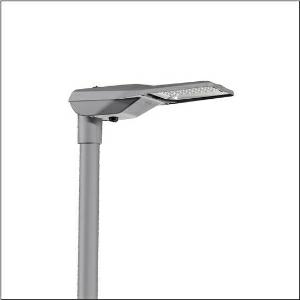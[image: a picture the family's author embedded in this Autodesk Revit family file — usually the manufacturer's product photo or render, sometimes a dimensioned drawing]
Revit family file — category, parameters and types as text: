
# Revit family: streetlight_sl_21_iq_mini___p0_8ab_5xe2r31y08gb_b9a0
name_source: partatom
category: Lighting Fixtures
units: mm (PartAtom-declared; Revit-internal decimal feet)

## family parameters
Cut with Voids When Loaded = No
Host = Face
Light Source = No
Part Type = Normal
Room Calculation Point = No
Round Connector Dimension = Use Diameter
Shared = No

## types (1)
- --- (1 x LED, 5200 lm, 39.8 W, 3000K)
    Apparent Load = 40 VA
    CIE Flux Codes = 36 71 98 100 100
    Color Rendering = 70
    Color Temperature = 3000K
    Default Elevation = 1800 mm
    Description = Streetlight SL 21 iQ mini, mast luminaire, primary light control with lens, of PMMA, primary optical cover: cover, of toughened safety glass, transparent, light distribution: P0.8aB, light emission: direct distribution, primary light characteristic: asymmetric, installation type: post-top, side-entry, LED, High Power LED, rated luminous flux: 5.200lm, luminous efficacy: 131lm/W, light colour: 730, colour temperature: 3000K, control gear: iQ-Street Remote, D4i with power reduction, control: pre-setting: logarithmic dimming characteristic, Street-Remote, Auto-Match, Temp-Guard, Lumen-Switch, Night-Set, Smart-Wire, Light-Fading, Desk-Remote (wireless, voltage-free reading and setting of iQ features in the workshop via application-optimized NFC function/RFID function), optimised constant luminous flux control (CLO 2.0), mains connection: 220..240V, AC, 50/60Hz, start of lifetime: 40W, end of service life: 41W, reduction: 18W, luminaire housing, of diecast aluminium, powder-coated, Siteco® metallic grey (DB 702S), corrosivity category C5 mid according to DIN EN ISO 12944, please order mast flange separately, inclination adjustable: 0°, 5°, 10°, 15°, sealing non-destructively replaceable, multi-level sealing system, length: 628mm, width: 235mm, height: 110mm, mast flange for spigot size: 42mm (side-entry): 5XC10008XM4, 60/48mm (side-entry/post-top): 5XC10108XM2, 76/60mm (side-entry/post-top): 5XC10108XM1, mounting height: 4..8m, Smart Interface below and above, protection rating (complete): IP66, insulation class (complete): insulation class II (safety insulation), certification: CE, ENEC, ENEC+, VDE, impact resistance: IK09, permissible operating ambient temperature for outdoor applications: -40..+50°C, standard-compliant lighting for roads and squares, packaging unit: 1 piece

Light Distribution: P0.8aB
    Height = 110 mm
    Lamp = 1 x LED
    Lamp Light Flux = 5200 lm
    Lamp Power = 39.8 W
    Lamp count = 1
    Length = 625 mm
    Luminous efficacy = 131 lm/W
    Manufacturer = Siteco
    ModVariant = No
    Model = 5XE2R31Y08GB
    Number of Poles = 1
    OnlyDefault = Yes
    Power Factor = 1
    Product Name = Streetlight SL 21 iQ mini | P0.8aB
    Product group = mast luminaire | pylon top
    ProductGroupID = 6100
    Protection Class = Protection class II
    Protection Degree = IP 66
    RLX_Detail_Level = 1
    RLX_Emergency_Light_Flux = 0 lm
    RLX_Emergency_Type = 0
    RLX_Emergency_Type_DB = No
    RlxData = <blob elided: 92561 chars, md5=5289aa6f>
    Socket = socket
    Standby Power = 0 W
    System Light Flux = 5200 lm
    System Power = 40 W
    Type Comments = factory setting: luminous flux: 100 % | dim-lin: 254 | 800 mA
    Type Image = l_1003514.jpg
    URL = http://relux.com
    VarID = @adj_072536
    Voltage = 0 V
    Weight = 0.00 kg
    Width = 234 mm

## geometry (parser evidence)
native form markers: Blend x4, Sweep x12
no freeform markers — native parametric forms only
